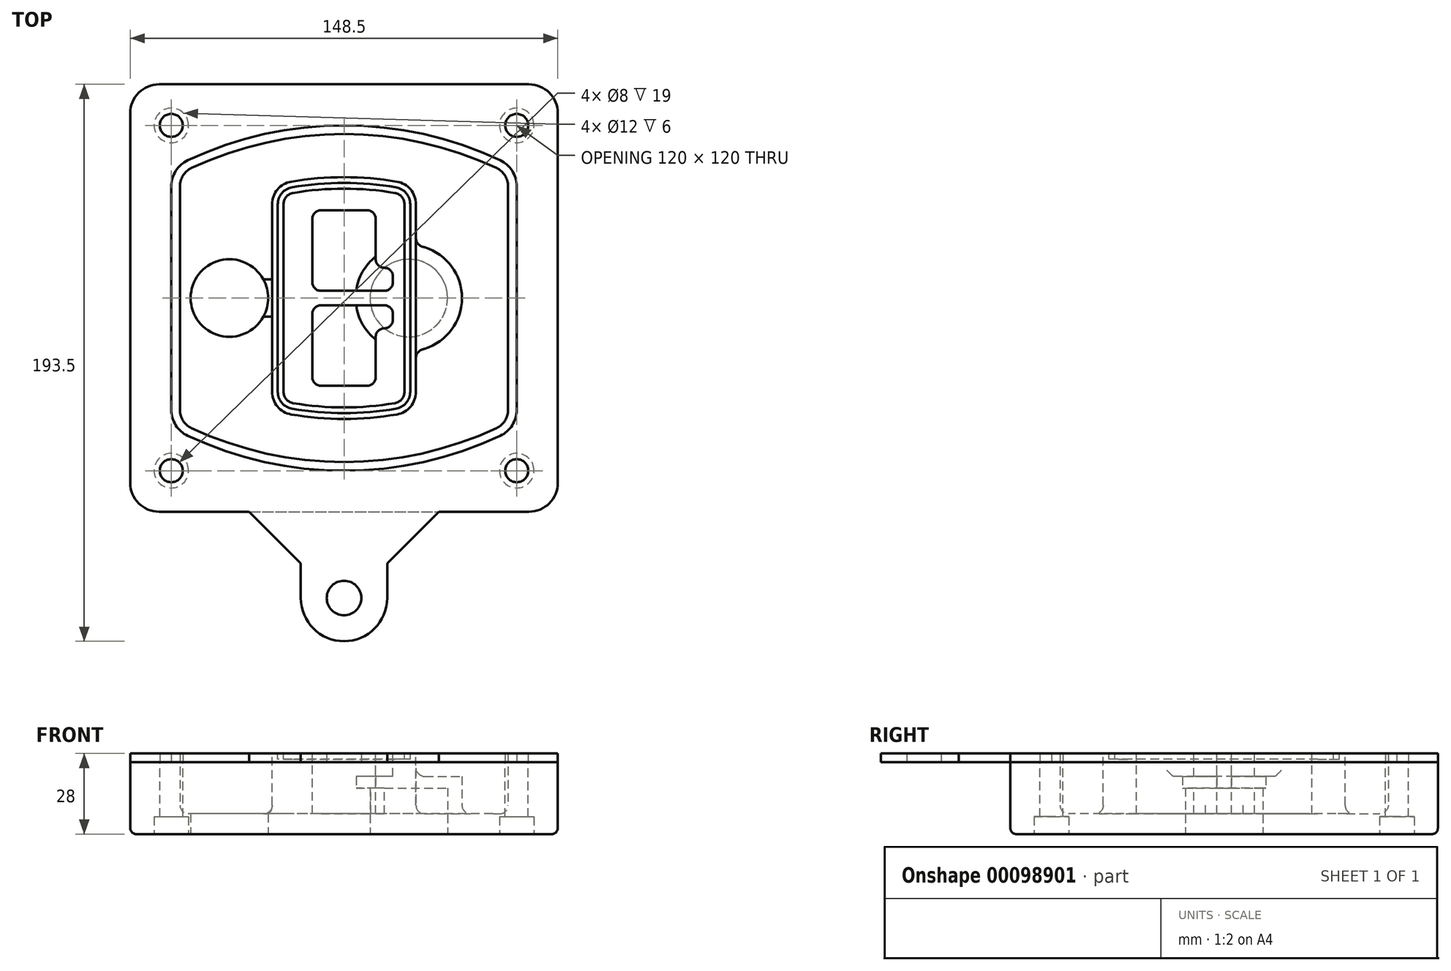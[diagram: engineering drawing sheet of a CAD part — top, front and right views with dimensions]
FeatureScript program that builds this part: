
annotation { "Feature Type Name" : "Feature", "Feature Type Description" : "" }
export const myFeature = defineFeature(function(context is Context, id is Id, definition is map)
    precondition{}
    {
        {
            var Q0;
            Q0=qCreatedBy(makeId("Top.planeOp"),FACE);
            var sketch = newSketch(context, id + "F0", { "sketchPlane" : qUnion([Q0])});
            skPoint(sketch, "E0.rect.middle", {"position": v(0, 0) * mm});
            skLineSegment(sketch, "E1.bottom", {"start": v(-64.25, -74.25) * mm, "end": v(64.25, -74.25) * mm});
            skLineSegment(sketch, "E1.top", {"start": v(-64.25, 74.25) * mm, "end": v(64.25, 74.25) * mm});
            skLineSegment(sketch, "E1.left", {"start": v(-74.25, -64.25) * mm, "end": v(-74.25, 64.25) * mm});
            skLineSegment(sketch, "E1.right", {"start": v(74.25, -64.25) * mm, "end": v(74.25, 64.25) * mm});
            skLineSegment(sketch, "E2", {"start": v(-74.25, 74.25) * mm, "end": v(74.25, -74.25) * mm, "construction": true});
            skLineSegment(sketch, "E3", {"start": v(74.25, 74.25) * mm, "end": v(-74.25, -74.25) * mm, "construction": true});
            skCircle(sketch, "E4", {"center": v(-60, 60) * mm, "radius": 4 * mm});
            skCircle(sketch, "E5", {"center": v(60, 60) * mm, "radius": 4 * mm});
            skCircle(sketch, "E6", {"center": v(60, -60) * mm, "radius": 4 * mm});
            skCircle(sketch, "E7", {"center": v(-60, -60) * mm, "radius": 4 * mm});
            skLineSegment(sketch, "E8", {"start": v(-60, 60) * mm, "end": v(60, 60) * mm, "construction": true});
            skLineSegment(sketch, "E9", {"start": v(60, 60) * mm, "end": v(60, -60) * mm, "construction": true});
            skLineSegment(sketch, "E10", {"start": v(60, -60) * mm, "end": v(-60, -60) * mm, "construction": true});
            skLineSegment(sketch, "E11", {"start": v(-60, -60) * mm, "end": v(-60, 60) * mm, "construction": true});
            skLineSegment(sketch, "E12", {"start": v(-60, 38.83) * mm, "end": v(-60, -38.83) * mm});
            skLineSegment(sketch, "E13", {"start": v(60, 38.83) * mm, "end": v(60, -38.83) * mm});
            skArc(sketch, "E14", {"start": v(54.26, 47.88) * mm, "mid": v(0, 60) * mm, "end": v(-54.26, 47.88) * mm});
            skArc(sketch, "E15", {"start": v(-54.26, -47.88) * mm, "mid": v(0, -60) * mm, "end": v(54.26, -47.88) * mm});
            skLineSegment(sketch, "E16", {"start": v(-60, 0) * mm, "end": v(60, 0) * mm, "construction": true});
            skPoint(sketch, "E17.visualSharp", {"position": v(-60, -45) * mm});
            skArc(sketch, "E17.filletArc", {"start": v(-60, -38.83) * mm, "mid": v(-58.44, -44.2) * mm, "end": v(-54.26, -47.88) * mm});
            skPoint(sketch, "E18.visualSharp", {"position": v(-60, 45) * mm});
            skArc(sketch, "E18.filletArc", {"start": v(-54.26, 47.88) * mm, "mid": v(-58.44, 44.2) * mm, "end": v(-60, 38.83) * mm});
            skPoint(sketch, "E19.visualSharp", {"position": v(60, 45) * mm});
            skArc(sketch, "E19.filletArc", {"start": v(60, 38.83) * mm, "mid": v(58.44, 44.2) * mm, "end": v(54.26, 47.88) * mm});
            skPoint(sketch, "E20.visualSharp", {"position": v(60, -45) * mm});
            skArc(sketch, "E20.filletArc", {"start": v(54.26, -47.88) * mm, "mid": v(58.44, -44.2) * mm, "end": v(60, -38.83) * mm});
            skPoint(sketch, "E21.visualSharp", {"position": v(-74.25, 74.25) * mm});
            skArc(sketch, "E21.filletArc", {"start": v(-64.25, 74.25) * mm, "mid": v(-71.32, 71.32) * mm, "end": v(-74.25, 64.25) * mm});
            skPoint(sketch, "E22.visualSharp", {"position": v(74.25, 74.25) * mm});
            skArc(sketch, "E22.filletArc", {"start": v(74.25, 64.25) * mm, "mid": v(71.32, 71.32) * mm, "end": v(64.25, 74.25) * mm});
            skPoint(sketch, "E23.visualSharp", {"position": v(74.25, -74.25) * mm});
            skArc(sketch, "E23.filletArc", {"start": v(64.25, -74.25) * mm, "mid": v(71.32, -71.32) * mm, "end": v(74.25, -64.25) * mm});
            skPoint(sketch, "E24.visualSharp", {"position": v(-74.25, -74.25) * mm});
            skArc(sketch, "E24.filletArc", {"start": v(-74.25, -64.25) * mm, "mid": v(-71.32, -71.32) * mm, "end": v(-64.25, -74.25) * mm});
            skArc(sketch, "E25.0", {"start": v(57, 38.83) * mm, "mid": v(55.9, 42.58) * mm, "end": v(52.98, 45.17) * mm});
            skLineSegment(sketch, "E25.1", {"start": v(57, 38.83) * mm, "end": v(57, -38.83) * mm});
            skArc(sketch, "E25.2", {"start": v(52.98, -45.17) * mm, "mid": v(55.9, -42.58) * mm, "end": v(57, -38.83) * mm});
            skArc(sketch, "E25.3", {"start": v(-52.98, -45.17) * mm, "mid": v(0, -57) * mm, "end": v(52.98, -45.17) * mm});
            skArc(sketch, "E25.4", {"start": v(-57, -38.83) * mm, "mid": v(-55.9, -42.58) * mm, "end": v(-52.98, -45.17) * mm});
            skArc(sketch, "E25.5", {"start": v(52.98, 45.17) * mm, "mid": v(0, 57) * mm, "end": v(-52.98, 45.17) * mm});
            skLineSegment(sketch, "E25.6", {"start": v(-57, 38.83) * mm, "end": v(-57, -38.83) * mm});
            skArc(sketch, "E25.7", {"start": v(-52.98, 45.17) * mm, "mid": v(-55.9, 42.58) * mm, "end": v(-57, 38.83) * mm});
            skArc(sketch, "E26.0", {"start": v(-55.96, 51.5) * mm, "mid": v(-61.82, 46.33) * mm, "end": v(-64, 38.83) * mm});
            skArc(sketch, "E26.1", {"start": v(55.96, 51.5) * mm, "mid": v(0, 64) * mm, "end": v(-55.96, 51.5) * mm});
            skArc(sketch, "E26.2", {"start": v(64, 38.83) * mm, "mid": v(61.82, 46.33) * mm, "end": v(55.96, 51.5) * mm});
            skLineSegment(sketch, "E26.3", {"start": v(64, 38.83) * mm, "end": v(64, -38.83) * mm});
            skArc(sketch, "E26.4", {"start": v(55.96, -51.5) * mm, "mid": v(61.82, -46.33) * mm, "end": v(64, -38.83) * mm});
            skLineSegment(sketch, "E26.5", {"start": v(-64, 38.83) * mm, "end": v(-64, -38.83) * mm});
            skArc(sketch, "E26.6", {"start": v(-55.96, -51.5) * mm, "mid": v(0, -64) * mm, "end": v(55.96, -51.5) * mm});
            skArc(sketch, "E26.7", {"start": v(-64, -38.83) * mm, "mid": v(-61.82, -46.33) * mm, "end": v(-55.96, -51.5) * mm});
            skSolve(sketch);
        }
        {
            var Q0;
            Q0=makeQuery(id+"F0.imprint","IMPRINT",FACE,{"disambiguationData":[TD([[makeQuery(id+"F0.imprint","IMPRINT",EDGE,{"derivedFrom":sQuery(id+"F0.wireOp",EDGE,"E1.bottom")}),1.0]])]});
            var Q1;
            Q1=makeQuery(id+"F0.imprint","IMPRINT",FACE,{"disambiguationData":[TD([[makeQuery(id+"F0.imprint","IMPRINT",EDGE,{"derivedFrom":sQuery(id+"F0.wireOp",EDGE,"E12")}),1.0]])]});
            var Q2;
            Q2=makeQuery(id+"F0.imprint","IMPRINT",FACE,{"disambiguationData":[TD([[makeQuery(id+"F0.imprint","IMPRINT",EDGE,{"derivedFrom":sQuery(id+"F0.wireOp",EDGE,"E25.0")}),1.0]])]});
            var Q3;
            Q3=makeQuery(id+"F0.imprint","IMPRINT",FACE,{"disambiguationData":[TD([[makeQuery(id+"F0.imprint","IMPRINT",EDGE,{"derivedFrom":sQuery(id+"F0.wireOp",EDGE,"E12")}),-1.0]])]});
            extrude(context, id + "F1", {"entities" : qUnion([Q0, Q1, Q2, Q3]), "oppositeDirection" : true, "depth" : 25 * mm});
        }
        {
            var Q0;
            Q0=makeQuery(id+"F0.imprint","IMPRINT",FACE,{"disambiguationData":[TD([[makeQuery(id+"F0.imprint","IMPRINT",EDGE,{"derivedFrom":sQuery(id+"F0.wireOp",EDGE,"E12")}),1.0]])]});
            extrude(context, id + "F2", {"entities" : qUnion([Q0]), "operationType" : NewBodyOperationType.ADD, "depth" : 3 * mm});
        }
        {
            var Q0;
            Q0=makeQuery(id+"F0.imprint","IMPRINT",FACE,{"disambiguationData":[TD([[makeQuery(id+"F0.imprint","IMPRINT",EDGE,{"derivedFrom":sQuery(id+"F0.wireOp",EDGE,"E25.0")}),1.0]])]});
            extrude(context, id + "F3", {"entities" : qUnion([Q0]), "operationType" : NewBodyOperationType.REMOVE, "oppositeDirection" : true, "depth" : 18 * mm});
        }
        {
            var Q0;
            Q0=makeQuery(id+"F2.opExtrude","CAP_FACE",FACE,{"disambiguationData":[OSD([sQuery(id+"F0.wireOp",EDGE,"E12"),sQuery(id+"F0.wireOp",EDGE,"E13"),sQuery(id+"F0.wireOp",EDGE,"E14"),sQuery(id+"F0.wireOp",EDGE,"E15"),sQuery(id+"F0.wireOp",EDGE,"E17.filletArc"),sQuery(id+"F0.wireOp",EDGE,"E18.filletArc"),sQuery(id+"F0.wireOp",EDGE,"E19.filletArc"),sQuery(id+"F0.wireOp",EDGE,"E20.filletArc"),sQuery(id+"F0.wireOp",EDGE,"E25.0"),sQuery(id+"F0.wireOp",EDGE,"E25.1"),sQuery(id+"F0.wireOp",EDGE,"E25.2"),sQuery(id+"F0.wireOp",EDGE,"E25.3"),sQuery(id+"F0.wireOp",EDGE,"E25.4"),sQuery(id+"F0.wireOp",EDGE,"E25.5"),sQuery(id+"F0.wireOp",EDGE,"E25.6"),sQuery(id+"F0.wireOp",EDGE,"E25.7")])],"isStart":false});
            var sketch = newSketch(context, id + "F4", { "sketchPlane" : qUnion([Q0])});
            skArc(sketch, "E27.0", {"start": v(-18.34, -40.45) * mm, "mid": v(0, -42) * mm, "end": v(18.34, -40.45) * mm});
            skArc(sketch, "E28.0", {"start": v(18.34, 40.45) * mm, "mid": v(0, 42) * mm, "end": v(-18.34, 40.45) * mm});
            skLineSegment(sketch, "E29", {"start": v(-25, 32.57) * mm, "end": v(-25, -32.57) * mm});
            skLineSegment(sketch, "E30", {"start": v(25, 32.57) * mm, "end": v(25, -32.57) * mm});
            skLineSegment(sketch, "E31", {"start": v(-25, 39.1) * mm, "end": v(25, 39.1) * mm, "construction": true});
            skLineSegment(sketch, "E32", {"start": v(-25, -39.1) * mm, "end": v(25, -39.1) * mm, "construction": true});
            skPoint(sketch, "E33.visualSharp", {"position": v(-25, 39.1) * mm});
            skArc(sketch, "E33.filletArc", {"start": v(-18.34, 40.45) * mm, "mid": v(-23.11, 37.73) * mm, "end": v(-25, 32.57) * mm});
            skPoint(sketch, "E34.visualSharp", {"position": v(25, 39.1) * mm});
            skArc(sketch, "E34.filletArc", {"start": v(25, 32.57) * mm, "mid": v(23.11, 37.73) * mm, "end": v(18.34, 40.45) * mm});
            skPoint(sketch, "E35.visualSharp", {"position": v(25, -39.1) * mm});
            skArc(sketch, "E35.filletArc", {"start": v(18.34, -40.45) * mm, "mid": v(23.11, -37.73) * mm, "end": v(25, -32.57) * mm});
            skPoint(sketch, "E36.visualSharp", {"position": v(-25, -39.1) * mm});
            skArc(sketch, "E36.filletArc", {"start": v(-25, -32.57) * mm, "mid": v(-23.11, -37.73) * mm, "end": v(-18.34, -40.45) * mm});
            skArc(sketch, "E37.0", {"start": v(52.98, 45.17) * mm, "mid": v(0, 57) * mm, "end": v(-52.98, 45.17) * mm});
            skArc(sketch, "E37.1", {"start": v(-52.98, 45.17) * mm, "mid": v(-55.9, 42.58) * mm, "end": v(-57, 38.83) * mm});
            skLineSegment(sketch, "E37.2", {"start": v(-57, 38.83) * mm, "end": v(-57, -38.83) * mm});
            skArc(sketch, "E37.3", {"start": v(-57, -38.83) * mm, "mid": v(-55.9, -42.58) * mm, "end": v(-52.98, -45.17) * mm});
            skArc(sketch, "E37.4", {"start": v(-52.98, -45.17) * mm, "mid": v(0, -57) * mm, "end": v(52.98, -45.17) * mm});
            skArc(sketch, "E37.5", {"start": v(52.98, -45.17) * mm, "mid": v(55.9, -42.58) * mm, "end": v(57, -38.83) * mm});
            skLineSegment(sketch, "E37.6", {"start": v(57, 38.83) * mm, "end": v(57, -38.83) * mm});
            skArc(sketch, "E37.7", {"start": v(57, 38.83) * mm, "mid": v(55.9, 42.58) * mm, "end": v(52.98, 45.17) * mm});
            skLineSegment(sketch, "E38.0", {"start": v(23, 32.57) * mm, "end": v(23, -32.57) * mm});
            skArc(sketch, "E38.1", {"start": v(18, -38.48) * mm, "mid": v(21.58, -36.44) * mm, "end": v(23, -32.57) * mm});
            skArc(sketch, "E38.2", {"start": v(-18, -38.48) * mm, "mid": v(0, -40) * mm, "end": v(18, -38.48) * mm});
            skArc(sketch, "E38.3", {"start": v(-23, -32.57) * mm, "mid": v(-21.58, -36.44) * mm, "end": v(-18, -38.48) * mm});
            skLineSegment(sketch, "E38.4", {"start": v(-23, 32.57) * mm, "end": v(-23, -32.57) * mm});
            skArc(sketch, "E38.5", {"start": v(23, 32.57) * mm, "mid": v(21.58, 36.44) * mm, "end": v(18, 38.48) * mm});
            skArc(sketch, "E38.6", {"start": v(-18, 38.48) * mm, "mid": v(-21.58, 36.44) * mm, "end": v(-23, 32.57) * mm});
            skArc(sketch, "E38.7", {"start": v(18, 38.48) * mm, "mid": v(0, 40) * mm, "end": v(-18, 38.48) * mm});
            skArc(sketch, "E39.0", {"start": v(21, 32.57) * mm, "mid": v(20.06, 35.15) * mm, "end": v(17.67, 36.5) * mm});
            skLineSegment(sketch, "E39.1", {"start": v(21, 32.57) * mm, "end": v(21, -32.57) * mm});
            skArc(sketch, "E39.2", {"start": v(17.67, -36.5) * mm, "mid": v(20.06, -35.15) * mm, "end": v(21, -32.57) * mm});
            skArc(sketch, "E39.3", {"start": v(-17.67, -36.5) * mm, "mid": v(0, -38) * mm, "end": v(17.67, -36.5) * mm});
            skArc(sketch, "E39.4", {"start": v(-21, -32.57) * mm, "mid": v(-20.06, -35.15) * mm, "end": v(-17.67, -36.5) * mm});
            skArc(sketch, "E39.5", {"start": v(17.67, 36.5) * mm, "mid": v(0, 38) * mm, "end": v(-17.67, 36.5) * mm});
            skLineSegment(sketch, "E39.6", {"start": v(-21, 32.57) * mm, "end": v(-21, -32.57) * mm});
            skArc(sketch, "E39.7", {"start": v(-17.67, 36.5) * mm, "mid": v(-20.06, 35.15) * mm, "end": v(-21, 32.57) * mm});
            skLineSegment(sketch, "E40", {"start": v(-25, 0) * mm, "end": v(25, 0) * mm, "construction": true});
            skLineSegment(sketch, "E41", {"start": v(-11, 5.5) * mm, "end": v(-11, 27.5) * mm});
            skLineSegment(sketch, "E42", {"start": v(-8, 30.5) * mm, "end": v(8, 30.5) * mm});
            skLineSegment(sketch, "E43", {"start": v(11, 27.5) * mm, "end": v(11, 13.5) * mm});
            skLineSegment(sketch, "E44", {"start": v(14, 10.5) * mm, "end": v(14, 10.5) * mm});
            skLineSegment(sketch, "E45", {"start": v(17, 7.5) * mm, "end": v(17, 5.5) * mm});
            skLineSegment(sketch, "E46", {"start": v(14, 2.5) * mm, "end": v(-8, 2.5) * mm});
            skPoint(sketch, "E47.visualSharp", {"position": v(-11, 30.5) * mm});
            skArc(sketch, "E47.filletArc", {"start": v(-8, 30.5) * mm, "mid": v(-10.12, 29.62) * mm, "end": v(-11, 27.5) * mm});
            skPoint(sketch, "E48.visualSharp", {"position": v(11, 30.5) * mm});
            skArc(sketch, "E48.filletArc", {"start": v(11, 27.5) * mm, "mid": v(10.12, 29.62) * mm, "end": v(8, 30.5) * mm});
            skPoint(sketch, "E49.visualSharp", {"position": v(11, 10.5) * mm});
            skArc(sketch, "E49.filletArc", {"start": v(11, 13.5) * mm, "mid": v(11.88, 11.38) * mm, "end": v(14, 10.5) * mm});
            skPoint(sketch, "E50.visualSharp", {"position": v(17, 10.5) * mm});
            skArc(sketch, "E50.filletArc", {"start": v(17, 7.5) * mm, "mid": v(16.12, 9.62) * mm, "end": v(14, 10.5) * mm});
            skPoint(sketch, "E51.visualSharp", {"position": v(17, 2.5) * mm});
            skArc(sketch, "E51.filletArc", {"start": v(14, 2.5) * mm, "mid": v(16.12, 3.38) * mm, "end": v(17, 5.5) * mm});
            skPoint(sketch, "E52.visualSharp", {"position": v(-11, 2.5) * mm});
            skArc(sketch, "E52.filletArc", {"start": v(-11, 5.5) * mm, "mid": v(-10.12, 3.38) * mm, "end": v(-8, 2.5) * mm});
            skLineSegment(sketch, "E53.0.MirrorCS", {"start": v(14, -2.5) * mm, "end": v(-8, -2.5) * mm});
            skArc(sketch, "E54.0.MirrorCS", {"start": v(-11, -5.5) * mm, "mid": v(-10.12, -3.38) * mm, "end": v(-8, -2.5) * mm});
            skLineSegment(sketch, "E55.0.MirrorCS", {"start": v(-11, -5.5) * mm, "end": v(-11, -27.5) * mm});
            skArc(sketch, "E56.0.MirrorCS", {"start": v(-8, -30.5) * mm, "mid": v(-10.12, -29.62) * mm, "end": v(-11, -27.5) * mm});
            skLineSegment(sketch, "E57.0.MirrorCS", {"start": v(-8, -30.5) * mm, "end": v(8, -30.5) * mm});
            skArc(sketch, "E58.0.MirrorCS", {"start": v(11, -27.5) * mm, "mid": v(10.12, -29.62) * mm, "end": v(8, -30.5) * mm});
            skLineSegment(sketch, "E59.0.MirrorCS", {"start": v(11, -27.5) * mm, "end": v(11, -13.5) * mm});
            skArc(sketch, "E60.0.MirrorCS", {"start": v(11, -13.5) * mm, "mid": v(11.88, -11.38) * mm, "end": v(14, -10.5) * mm});
            skArc(sketch, "E61.0.MirrorCS", {"start": v(17, -7.5) * mm, "mid": v(16.12, -9.62) * mm, "end": v(14, -10.5) * mm});
            skLineSegment(sketch, "E62.0.MirrorCS", {"start": v(17, -7.5) * mm, "end": v(17, -5.5) * mm});
            skArc(sketch, "E63.0.MirrorCS", {"start": v(14, -2.5) * mm, "mid": v(16.12, -3.38) * mm, "end": v(17, -5.5) * mm});
            skSolve(sketch);
        }
        {
            var Q0;
            Q0=makeQuery(id+"F4.imprint","IMPRINT",FACE,{"disambiguationData":[TD([[makeQuery(id+"F4.imprint","IMPRINT",EDGE,{"derivedFrom":sQuery(id+"F4.wireOp",EDGE,"E27.0")}),1.0]])]});
            var Q1;
            Q1=makeQuery(id+"F4.imprint","IMPRINT",FACE,{"disambiguationData":[TD([[makeQuery(id+"F4.imprint","IMPRINT",EDGE,{"derivedFrom":sQuery(id+"F4.wireOp",EDGE,"E38.0")}),-1.0]])]});
            var Q2;
            Q2=makeQuery(id+"F4.imprint","IMPRINT",FACE,{"disambiguationData":[TD([[makeQuery(id+"F4.imprint","IMPRINT",EDGE,{"derivedFrom":sQuery(id+"F4.wireOp",EDGE,"E39.0")}),1.0]])]});
            extrude(context, id + "F5", {"entities" : qUnion([Q0, Q1, Q2]), "operationType" : NewBodyOperationType.ADD, "endBound" : BoundingType.UP_TO_NEXT, "oppositeDirection" : true, "depth" : 25 * mm});
        }
        {
            var Q0;
            Q0=makeQuery(id+"F4.imprint","IMPRINT",FACE,{"disambiguationData":[TD([[makeQuery(id+"F4.imprint","IMPRINT",EDGE,{"derivedFrom":sQuery(id+"F4.wireOp",EDGE,"E38.0")}),-1.0]])]});
            extrude(context, id + "F6", {"entities" : qUnion([Q0]), "operationType" : NewBodyOperationType.REMOVE, "oppositeDirection" : true, "depth" : 2 * mm});
        }
        {
            var Q0;
            Q0=makeQuery(id+"F1.opExtrude","CAP_FACE",FACE,{"disambiguationData":[OSD([sQuery(id+"F0.wireOp",EDGE,"E1.bottom"),sQuery(id+"F0.wireOp",EDGE,"E1.top"),sQuery(id+"F0.wireOp",EDGE,"E1.left"),sQuery(id+"F0.wireOp",EDGE,"E1.right"),sQuery(id+"F0.wireOp",EDGE,"E4"),sQuery(id+"F0.wireOp",EDGE,"E5"),sQuery(id+"F0.wireOp",EDGE,"E6"),sQuery(id+"F0.wireOp",EDGE,"E7"),sQuery(id+"F0.wireOp",EDGE,"E21.filletArc"),sQuery(id+"F0.wireOp",EDGE,"E22.filletArc"),sQuery(id+"F0.wireOp",EDGE,"E23.filletArc"),sQuery(id+"F0.wireOp",EDGE,"E24.filletArc")])],"isStart":false});
            var sketch = newSketch(context, id + "F7", { "sketchPlane" : qUnion([Q0])});
            skCircle(sketch, "E64", {"center": v(22.5, 0) * mm, "radius": 13.47 * mm});
            skCircle(sketch, "E65", {"center": v(-39.81, 0) * mm, "radius": 13.47 * mm});
            skLineSegment(sketch, "E66", {"start": v(74.25, 0) * mm, "end": v(-74.25, 0) * mm});
            skCircle(sketch, "E67", {"center": v(22.5, 0) * mm, "radius": 18.47 * mm});
            skCircle(sketch, "E68", {"center": v(60, -60) * mm, "radius": 6 * mm});
            skCircle(sketch, "E69", {"center": v(-60, -60) * mm, "radius": 6 * mm});
            skCircle(sketch, "E70", {"center": v(-60, 60) * mm, "radius": 6 * mm});
            skCircle(sketch, "E71", {"center": v(60, 60) * mm, "radius": 6 * mm});
            skSolve(sketch);
        }
        {
            var Q0;
            {var subQ1=sQuery(id+"F7.wireOp",EDGE,"E66");var subQ4=sQuery(id+"F7.wireOp",EDGE,"E64");var subQ6=makeQuery(id+"F7.imprint","INTERSECT",VERTEX,{"disambiguationData":[OD(0.0)],"derivedFrom":[subQ4,subQ1]});Q0=makeQuery(id+"F7.imprint","IMPRINT",FACE,{"disambiguationData":[TD([[makeQuery(id+"F7.imprint","IMPRINT",EDGE,{"disambiguationData":[TD([[subQ6,-1.0]])],"derivedFrom":subQ4}),-1.0]])]});}
            var Q1;
            {var subQ0=sQuery(id+"F7.wireOp",EDGE,"E66");var subQ1=sQuery(id+"F7.wireOp",EDGE,"E64");var subQ3=makeQuery(id+"F7.imprint","INTERSECT",VERTEX,{"disambiguationData":[OD(0.0)],"derivedFrom":[subQ1,subQ0]});Q1=makeQuery(id+"F7.imprint","IMPRINT",FACE,{"disambiguationData":[TD([[makeQuery(id+"F7.imprint","IMPRINT",EDGE,{"disambiguationData":[TD([[subQ3,-1.0]])],"derivedFrom":subQ1}),1.0]])]});}
            var Q2;
            {var subQ0=sQuery(id+"F7.wireOp",EDGE,"E66");var subQ1=sQuery(id+"F7.wireOp",EDGE,"E64");var subQ3=makeQuery(id+"F7.imprint","INTERSECT",VERTEX,{"disambiguationData":[OD(0.0)],"derivedFrom":[subQ1,subQ0]});Q2=makeQuery(id+"F7.imprint","IMPRINT",FACE,{"disambiguationData":[TD([[makeQuery(id+"F7.imprint","IMPRINT",EDGE,{"disambiguationData":[TD([[subQ3,1.0]])],"derivedFrom":subQ1}),1.0]])]});}
            var Q3;
            {var subQ1=sQuery(id+"F7.wireOp",EDGE,"E66");var subQ4=sQuery(id+"F7.wireOp",EDGE,"E64");var subQ6=makeQuery(id+"F7.imprint","INTERSECT",VERTEX,{"disambiguationData":[OD(0.0)],"derivedFrom":[subQ4,subQ1]});Q3=makeQuery(id+"F7.imprint","IMPRINT",FACE,{"disambiguationData":[TD([[makeQuery(id+"F7.imprint","IMPRINT",EDGE,{"disambiguationData":[TD([[subQ6,1.0]])],"derivedFrom":subQ4}),-1.0]])]});}
            extrude(context, id + "F8", {"entities" : qUnion([Q0, Q1, Q2, Q3]), "operationType" : NewBodyOperationType.ADD, "oppositeDirection" : true, "depth" : 20 * mm});
        }
        {
            var Q0;
            {var subQ0=sQuery(id+"F7.wireOp",EDGE,"E66");var subQ1=sQuery(id+"F7.wireOp",EDGE,"E64");var subQ3=makeQuery(id+"F7.imprint","INTERSECT",VERTEX,{"disambiguationData":[OD(0.0)],"derivedFrom":[subQ1,subQ0]});Q0=makeQuery(id+"F7.imprint","IMPRINT",FACE,{"disambiguationData":[TD([[makeQuery(id+"F7.imprint","IMPRINT",EDGE,{"disambiguationData":[TD([[subQ3,-1.0]])],"derivedFrom":subQ1}),1.0]])]});}
            var Q1;
            {var subQ0=sQuery(id+"F7.wireOp",EDGE,"E66");var subQ1=sQuery(id+"F7.wireOp",EDGE,"E64");var subQ3=makeQuery(id+"F7.imprint","INTERSECT",VERTEX,{"disambiguationData":[OD(0.0)],"derivedFrom":[subQ1,subQ0]});Q1=makeQuery(id+"F7.imprint","IMPRINT",FACE,{"disambiguationData":[TD([[makeQuery(id+"F7.imprint","IMPRINT",EDGE,{"disambiguationData":[TD([[subQ3,1.0]])],"derivedFrom":subQ1}),1.0]])]});}
            extrude(context, id + "F9", {"entities" : qUnion([Q0, Q1]), "operationType" : NewBodyOperationType.REMOVE, "oppositeDirection" : true, "depth" : 16 * mm});
        }
        {
            var Q0;
            {var subQ0=sQuery(id+"F7.wireOp",EDGE,"E66");var subQ1=sQuery(id+"F7.wireOp",EDGE,"E65");var subQ3=makeQuery(id+"F7.imprint","INTERSECT",VERTEX,{"disambiguationData":[OD(0.0)],"derivedFrom":[subQ1,subQ0]});Q0=makeQuery(id+"F7.imprint","IMPRINT",FACE,{"disambiguationData":[TD([[makeQuery(id+"F7.imprint","IMPRINT",EDGE,{"disambiguationData":[TD([[subQ3,-1.0]])],"derivedFrom":subQ1}),1.0]])]});}
            var Q1;
            {var subQ0=sQuery(id+"F7.wireOp",EDGE,"E66");var subQ1=sQuery(id+"F7.wireOp",EDGE,"E65");var subQ3=makeQuery(id+"F7.imprint","INTERSECT",VERTEX,{"disambiguationData":[OD(0.0)],"derivedFrom":[subQ1,subQ0]});Q1=makeQuery(id+"F7.imprint","IMPRINT",FACE,{"disambiguationData":[TD([[makeQuery(id+"F7.imprint","IMPRINT",EDGE,{"disambiguationData":[TD([[subQ3,1.0]])],"derivedFrom":subQ1}),1.0]])]});}
            extrude(context, id + "F10", {"entities" : qUnion([Q0, Q1]), "operationType" : NewBodyOperationType.REMOVE, "oppositeDirection" : true, "depth" : 25 * mm});
        }
        {
            var Q0;
            Q0=makeQuery(id+"F7.imprint","IMPRINT",FACE,{"disambiguationData":[TD([[makeQuery(id+"F7.imprint","IMPRINT",EDGE,{"derivedFrom":sQuery(id+"F7.wireOp",EDGE,"E68")}),1.0]])]});
            var Q1;
            Q1=makeQuery(id+"F7.imprint","IMPRINT",FACE,{"disambiguationData":[TD([[makeQuery(id+"F7.imprint","IMPRINT",EDGE,{"derivedFrom":makeQuery(id+"F1.opExtrude","CAP_EDGE",EDGE,{"disambiguationData":[OSD([sQuery(id+"F0.wireOp",EDGE,"E5")])],"isStart":false})}),-1.0]])]});
            var Q2;
            Q2=makeQuery(id+"F7.imprint","IMPRINT",FACE,{"disambiguationData":[TD([[makeQuery(id+"F7.imprint","IMPRINT",EDGE,{"derivedFrom":sQuery(id+"F7.wireOp",EDGE,"E69")}),1.0]])]});
            var Q3;
            Q3=makeQuery(id+"F7.imprint","IMPRINT",FACE,{"disambiguationData":[TD([[makeQuery(id+"F7.imprint","IMPRINT",EDGE,{"derivedFrom":makeQuery(id+"F1.opExtrude","CAP_EDGE",EDGE,{"disambiguationData":[OSD([sQuery(id+"F0.wireOp",EDGE,"E4")])],"isStart":false})}),-1.0]])]});
            var Q4;
            Q4=makeQuery(id+"F7.imprint","IMPRINT",FACE,{"disambiguationData":[TD([[makeQuery(id+"F7.imprint","IMPRINT",EDGE,{"derivedFrom":sQuery(id+"F7.wireOp",EDGE,"E70")}),1.0]])]});
            var Q5;
            Q5=makeQuery(id+"F7.imprint","IMPRINT",FACE,{"disambiguationData":[TD([[makeQuery(id+"F7.imprint","IMPRINT",EDGE,{"derivedFrom":makeQuery(id+"F1.opExtrude","CAP_EDGE",EDGE,{"disambiguationData":[OSD([sQuery(id+"F0.wireOp",EDGE,"E7")])],"isStart":false})}),-1.0]])]});
            var Q6;
            Q6=makeQuery(id+"F7.imprint","IMPRINT",FACE,{"disambiguationData":[TD([[makeQuery(id+"F7.imprint","IMPRINT",EDGE,{"derivedFrom":sQuery(id+"F7.wireOp",EDGE,"E71")}),1.0]])]});
            var Q7;
            Q7=makeQuery(id+"F7.imprint","IMPRINT",FACE,{"disambiguationData":[TD([[makeQuery(id+"F7.imprint","IMPRINT",EDGE,{"derivedFrom":makeQuery(id+"F1.opExtrude","CAP_EDGE",EDGE,{"disambiguationData":[OSD([sQuery(id+"F0.wireOp",EDGE,"E6")])],"isStart":false})}),-1.0]])]});
            extrude(context, id + "F11", {"entities" : qUnion([Q0, Q1, Q2, Q3, Q4, Q5, Q6, Q7]), "operationType" : NewBodyOperationType.REMOVE, "oppositeDirection" : true, "depth" : 6 * mm});
        }
        {
            var Q0;
            Q0=makeQuery(id+"F9.boolean.opBoolean","COPY",FACE,{"derivedFrom":makeQuery(id+"F9.opExtrude","CAP_FACE",FACE,{"disambiguationData":[OSD([sQuery(id+"F7.wireOp",EDGE,"E64")])],"isStart":false})});
            var sketch = newSketch(context, id + "F12", { "sketchPlane" : qUnion([Q0])});
            skArc(sketch, "E72.0", {"start": v(11, 14.45) * mm, "mid": v(6.45, 9.13) * mm, "end": v(4.2, 2.5) * mm});
            skArc(sketch, "E72.1", {"start": v(4.2, -2.5) * mm, "mid": v(6.45, -9.13) * mm, "end": v(11, -14.45) * mm});
            skLineSegment(sketch, "E73", {"start": v(4.2, -2.5) * mm, "end": v(14, -2.5) * mm});
            skLineSegment(sketch, "E74.0", {"start": v(14, 2.5) * mm, "end": v(4.2, 2.5) * mm});
            skArc(sketch, "E74.1", {"start": v(14, 2.5) * mm, "mid": v(16.12, 3.38) * mm, "end": v(17, 5.5) * mm});
            skLineSegment(sketch, "E74.2", {"start": v(17, 7.5) * mm, "end": v(17, 5.5) * mm});
            skArc(sketch, "E74.3", {"start": v(17, 7.5) * mm, "mid": v(16.12, 9.62) * mm, "end": v(14, 10.5) * mm});
            skArc(sketch, "E74.4", {"start": v(11, 13.5) * mm, "mid": v(11.88, 11.38) * mm, "end": v(14, 10.5) * mm});
            skLineSegment(sketch, "E74.5", {"start": v(11, 14.45) * mm, "end": v(11, 13.5) * mm});
            skLineSegment(sketch, "E74.7", {"start": v(14, -2.5) * mm, "end": v(4.2, -2.5) * mm});
            skArc(sketch, "E74.8", {"start": v(14, -2.5) * mm, "mid": v(16.12, -3.38) * mm, "end": v(17, -5.5) * mm});
            skLineSegment(sketch, "E74.9", {"start": v(17, -7.5) * mm, "end": v(17, -5.5) * mm});
            skArc(sketch, "E74.10", {"start": v(17, -7.5) * mm, "mid": v(16.12, -9.62) * mm, "end": v(14, -10.5) * mm});
            skArc(sketch, "E74.11", {"start": v(11, -13.5) * mm, "mid": v(11.88, -11.38) * mm, "end": v(14, -10.5) * mm});
            skLineSegment(sketch, "E74.12", {"start": v(11, -14.45) * mm, "end": v(11, -13.5) * mm});
            skPoint(sketch, "E75.orphan", {"position": v(11, -27.5) * mm});
            skPoint(sketch, "E76.orphan", {"position": v(-8, -2.5) * mm});
            skPoint(sketch, "E77.orphan", {"position": v(-8, 2.5) * mm});
            skPoint(sketch, "E78.orphan", {"position": v(11, 27.5) * mm});
            skSolve(sketch);
        }
        {
            var Q0;
            {var subQ7=sQuery(id+"F12.wireOp",EDGE,"E72.0");var subQ14=sQuery(id+"F12.wireOp",EDGE,"E72.1");var subQ16=sQuery(id+"F12.wireOp",EDGE,"E74.1");var subQ18=sQuery(id+"F12.wireOp",EDGE,"E74.8");Q0=qUnion([makeQuery(id+"F12.imprint","IMPRINT",FACE,{"disambiguationData":[TD([[makeQuery(id+"F12.imprint","IMPRINT",EDGE,{"derivedFrom":subQ7}),1.0]])]}),makeQuery(id+"F12.imprint","IMPRINT",FACE,{"disambiguationData":[TD([[makeQuery(id+"F12.imprint","IMPRINT",EDGE,{"derivedFrom":subQ14}),1.0]])]}),makeQuery(id+"F12.imprint","IMPRINT",FACE,{"disambiguationData":[TD([[makeQuery(id+"F12.imprint","IMPRINT",EDGE,{"derivedFrom":subQ16}),1.0]])]}),makeQuery(id+"F12.imprint","IMPRINT",FACE,{"disambiguationData":[TD([[makeQuery(id+"F12.imprint","IMPRINT",EDGE,{"derivedFrom":subQ18}),-1.0]])]})]);}
            var Q1;
            Q1=makeQuery(id+"F5.boolean.opBoolean","SPLIT",FACE,{"disambiguationData":[TD([makeQuery(id+"F5.opExtrude","SWEPT_FACE",FACE,{"disambiguationData":[OSD([sQuery(id+"F4.wireOp",EDGE,"E41")])]})])],"derivedFrom":makeQuery(id+"F3.boolean.opBoolean","COPY",FACE,{"derivedFrom":makeQuery(id+"F3.opExtrude","CAP_FACE",FACE,{"disambiguationData":[OSD([sQuery(id+"F0.wireOp",EDGE,"E25.0"),sQuery(id+"F0.wireOp",EDGE,"E25.1"),sQuery(id+"F0.wireOp",EDGE,"E25.2"),sQuery(id+"F0.wireOp",EDGE,"E25.3"),sQuery(id+"F0.wireOp",EDGE,"E25.4"),sQuery(id+"F0.wireOp",EDGE,"E25.5"),sQuery(id+"F0.wireOp",EDGE,"E25.6"),sQuery(id+"F0.wireOp",EDGE,"E25.7")])],"isStart":false})})});
            extrude(context, id + "F13", {"entities" : qUnion([Q0]), "operationType" : NewBodyOperationType.REMOVE, "endBound" : BoundingType.UP_TO_SURFACE, "endBoundEntityFace" : qUnion([Q1]), "depth" : 25 * mm});
        }
        {
            var Q0;
            Q0=makeQuery(id+"F3.boolean.opBoolean","COPY",EDGE,{"derivedFrom":makeQuery(id+"F3.opExtrude","CAP_EDGE",EDGE,{"disambiguationData":[OSD([sQuery(id+"F0.wireOp",EDGE,"E25.6")])],"isStart":false})});
            var Q1;
            Q1=makeQuery(id+"F8.boolean.opBoolean","INTERSECT",EDGE,{"derivedFrom":[makeQuery(id+"F5.opExtrude","SWEPT_FACE",FACE,{"disambiguationData":[OSD([sQuery(id+"F4.wireOp",EDGE,"E30")])]}),makeQuery(id+"F8.opExtrude","CAP_FACE",FACE,{"disambiguationData":[OSD([sQuery(id+"F7.wireOp",EDGE,"E67")])],"isStart":false})]});
            var Q2;
            Q2=makeQuery(id+"F8.boolean.opBoolean","INTERSECT",EDGE,{"disambiguationData":[OD(1.0)],"derivedFrom":[makeQuery(id+"F5.opExtrude","SWEPT_FACE",FACE,{"disambiguationData":[OSD([sQuery(id+"F4.wireOp",EDGE,"E30")])]}),makeQuery(id+"F8.opExtrude","SWEPT_FACE",FACE,{"disambiguationData":[OSD([sQuery(id+"F7.wireOp",EDGE,"E67")])]})]});
            var Q3;
            {var subQ0=sQuery(id+"F4.wireOp",EDGE,"E30");Q3=makeQuery(id+"F8.boolean.opBoolean","SPLIT",EDGE,{"disambiguationData":[TD([makeQuery(id+"F5.opExtrude","SWEPT_FACE",FACE,{"disambiguationData":[OSD([sQuery(id+"F4.wireOp",EDGE,"E35.filletArc")])]})])],"derivedFrom":makeQuery(id+"F5.opExtrude","CAP_EDGE",EDGE,{"disambiguationData":[OSD([subQ0])],"isStart":false})});}
            var Q4;
            {var subQ0=sQuery(id+"F0.wireOp",EDGE,"E25.7");var subQ1=sQuery(id+"F0.wireOp",EDGE,"E25.1");var subQ2=sQuery(id+"F0.wireOp",EDGE,"E25.6");var subQ3=sQuery(id+"F0.wireOp",EDGE,"E25.5");var subQ4=sQuery(id+"F0.wireOp",EDGE,"E25.4");var subQ5=sQuery(id+"F0.wireOp",EDGE,"E25.0");var subQ6=sQuery(id+"F0.wireOp",EDGE,"E25.2");var subQ7=sQuery(id+"F0.wireOp",EDGE,"E25.3");Q4=makeQuery(id+"F8.boolean.opBoolean","INTERSECT",EDGE,{"derivedFrom":[makeQuery(id+"F5.boolean.opBoolean","SPLIT",FACE,{"disambiguationData":[TD([makeQuery(id+"F2.opExtrude","SWEPT_FACE",FACE,{"disambiguationData":[OSD([subQ5])]})])],"derivedFrom":makeQuery(id+"F3.boolean.opBoolean","COPY",FACE,{"derivedFrom":makeQuery(id+"F3.opExtrude","CAP_FACE",FACE,{"disambiguationData":[OSD([subQ5,subQ1,subQ6,subQ7,subQ4,subQ3,subQ2,subQ0])],"isStart":false})})}),makeQuery(id+"F8.opExtrude","SWEPT_FACE",FACE,{"disambiguationData":[OSD([sQuery(id+"F7.wireOp",EDGE,"E67")])]})]});}
            var Q5;
            Q5=makeQuery(id+"F8.boolean.opBoolean","INTERSECT",EDGE,{"disambiguationData":[OD(0.0)],"derivedFrom":[makeQuery(id+"F5.opExtrude","SWEPT_FACE",FACE,{"disambiguationData":[OSD([sQuery(id+"F4.wireOp",EDGE,"E30")])]}),makeQuery(id+"F8.opExtrude","SWEPT_FACE",FACE,{"disambiguationData":[OSD([sQuery(id+"F7.wireOp",EDGE,"E67")])]})]});
            fillet(context, id + "F14", {"entities" : qUnion([Q0, Q1, Q2, Q3, Q4, Q5]), "radius" : 3 * mm, "tangentPropagation" : true, "allowEdgeOverflow" : false});
        }
        {
            var Q0;
            Q0=makeQuery(id+"F1.opExtrude","CAP_EDGE",EDGE,{"disambiguationData":[OSD([sQuery(id+"F0.wireOp",EDGE,"E1.bottom")])],"isStart":false});
            fillet(context, id + "F15", {"entities" : qUnion([Q0]), "radius" : 2 * mm, "tangentPropagation" : true, "allowEdgeOverflow" : false});
        }
        {
            var Q0;
            {var subQ0=sQuery(id+"F0.wireOp",EDGE,"E22.filletArc");var subQ1=sQuery(id+"F0.wireOp",EDGE,"E7");var subQ2=sQuery(id+"F0.wireOp",EDGE,"E6");var subQ3=sQuery(id+"F0.wireOp",EDGE,"E5");var subQ4=sQuery(id+"F0.wireOp",EDGE,"E4");var subQ5=sQuery(id+"F0.wireOp",EDGE,"E1.bottom");var subQ6=sQuery(id+"F0.wireOp",EDGE,"E21.filletArc");var subQ7=sQuery(id+"F0.wireOp",EDGE,"E1.top");var subQ8=sQuery(id+"F0.wireOp",EDGE,"E1.left");var subQ9=sQuery(id+"F0.wireOp",EDGE,"E1.right");var subQ10=sQuery(id+"F0.wireOp",EDGE,"E23.filletArc");var subQ11=sQuery(id+"F0.wireOp",EDGE,"E24.filletArc");Q0=makeQuery(id+"F2.boolean.opBoolean","SPLIT",FACE,{"disambiguationData":[TD([makeQuery(id+"F1.opExtrude","SWEPT_FACE",FACE,{"disambiguationData":[OSD([subQ5])]})])],"derivedFrom":makeQuery(id+"F1.opExtrude","CAP_FACE",FACE,{"disambiguationData":[OSD([subQ5,subQ7,subQ8,subQ9,subQ4,subQ3,subQ2,subQ1,subQ6,subQ0,subQ10,subQ11])],"isStart":true})});}
            var sketch = newSketch(context, id + "F16", { "sketchPlane" : qUnion([Q0])});
            skLineSegment(sketch, "E79.0", {"start": v(-64.25, 74.25) * mm, "end": v(64.25, 74.25) * mm});
            skLineSegment(sketch, "E80", {"start": v(0, 74.25) * mm, "end": v(0, 104.25) * mm, "construction": true});
            skArc(sketch, "E81", {"start": v(-15, 104.25) * mm, "mid": v(0, 119.25) * mm, "end": v(15, 104.25) * mm});
            skLineSegment(sketch, "E82", {"start": v(15, 104.25) * mm, "end": v(15, 92.25) * mm});
            skLineSegment(sketch, "E83", {"start": v(15, 92.25) * mm, "end": v(33, 74.25) * mm});
            skLineSegment(sketch, "E84", {"start": v(0, 0) * mm, "end": v(-145.18, 0) * mm, "construction": true});
            skLineSegment(sketch, "E85", {"start": v(-15, 104.25) * mm, "end": v(-15, 92.25) * mm});
            skLineSegment(sketch, "E86", {"start": v(-15, 92.25) * mm, "end": v(-33, 74.25) * mm});
            skCircle(sketch, "E87", {"center": v(0, 104.25) * mm, "radius": 6 * mm});
            skLineSegment(sketch, "E88.MirrorCS", {"start": v(15, -92.25) * mm, "end": v(33, -74.25) * mm});
            skLineSegment(sketch, "E89.MirrorCS", {"start": v(15, -104.25) * mm, "end": v(15, -92.25) * mm});
            skArc(sketch, "E90.MirrorCS", {"start": v(-15, -104.25) * mm, "mid": v(0, -119.25) * mm, "end": v(15, -104.25) * mm});
            skCircle(sketch, "E91.MirrorC", {"center": v(0, -104.25) * mm, "radius": 6 * mm});
            skLineSegment(sketch, "E92.MirrorCS", {"start": v(-15, -104.25) * mm, "end": v(-15, -92.25) * mm});
            skLineSegment(sketch, "E93.MirrorCS", {"start": v(-15, -92.25) * mm, "end": v(-33, -74.25) * mm});
            skSolve(sketch);
        }
        {
            var Q0;
            Q0=makeQuery(id+"F16.imprint","IMPRINT",FACE,{"disambiguationData":[TD([[makeQuery(id+"F16.imprint","IMPRINT",EDGE,{"derivedFrom":sQuery(id+"F16.wireOp",EDGE,"E81")}),-1.0]])]});
            var Q1;
            Q1=makeQuery(id+"F16.imprint","IMPRINT",FACE,{"disambiguationData":[TD([[makeQuery(id+"F16.imprint","IMPRINT",EDGE,{"derivedFrom":makeQuery(id+"F1.opExtrude","CAP_EDGE",EDGE,{"disambiguationData":[OSD([sQuery(id+"F0.wireOp",EDGE,"E1.left")])],"isStart":true})}),-1.0]])]});
            var Q2;
            {var subQ0=sQuery(id+"F16.wireOp",EDGE,"E88.MirrorCS");Q2=makeQuery(id+"F16.imprint","IMPRINT",FACE,{"disambiguationData":[TD([[makeQuery(id+"F16.imprint","IMPRINT",EDGE,{"derivedFrom":subQ0}),1.0]])]});}
            var Q3;
            Q3=makeQuery(id+"F2.opExtrude","CAP_FACE",FACE,{"disambiguationData":[OSD([sQuery(id+"F0.wireOp",EDGE,"E12"),sQuery(id+"F0.wireOp",EDGE,"E13"),sQuery(id+"F0.wireOp",EDGE,"E14"),sQuery(id+"F0.wireOp",EDGE,"E15"),sQuery(id+"F0.wireOp",EDGE,"E17.filletArc"),sQuery(id+"F0.wireOp",EDGE,"E18.filletArc"),sQuery(id+"F0.wireOp",EDGE,"E19.filletArc"),sQuery(id+"F0.wireOp",EDGE,"E20.filletArc"),sQuery(id+"F0.wireOp",EDGE,"E25.0"),sQuery(id+"F0.wireOp",EDGE,"E25.1"),sQuery(id+"F0.wireOp",EDGE,"E25.2"),sQuery(id+"F0.wireOp",EDGE,"E25.3"),sQuery(id+"F0.wireOp",EDGE,"E25.4"),sQuery(id+"F0.wireOp",EDGE,"E25.5"),sQuery(id+"F0.wireOp",EDGE,"E25.6"),sQuery(id+"F0.wireOp",EDGE,"E25.7")])],"isStart":false});
            extrude(context, id + "F17", {"entities" : qUnion([Q0, Q1, Q2]), "endBound" : BoundingType.UP_TO_SURFACE, "endBoundEntityFace" : qUnion([Q3]), "depth" : 25 * mm});
        }
    });
